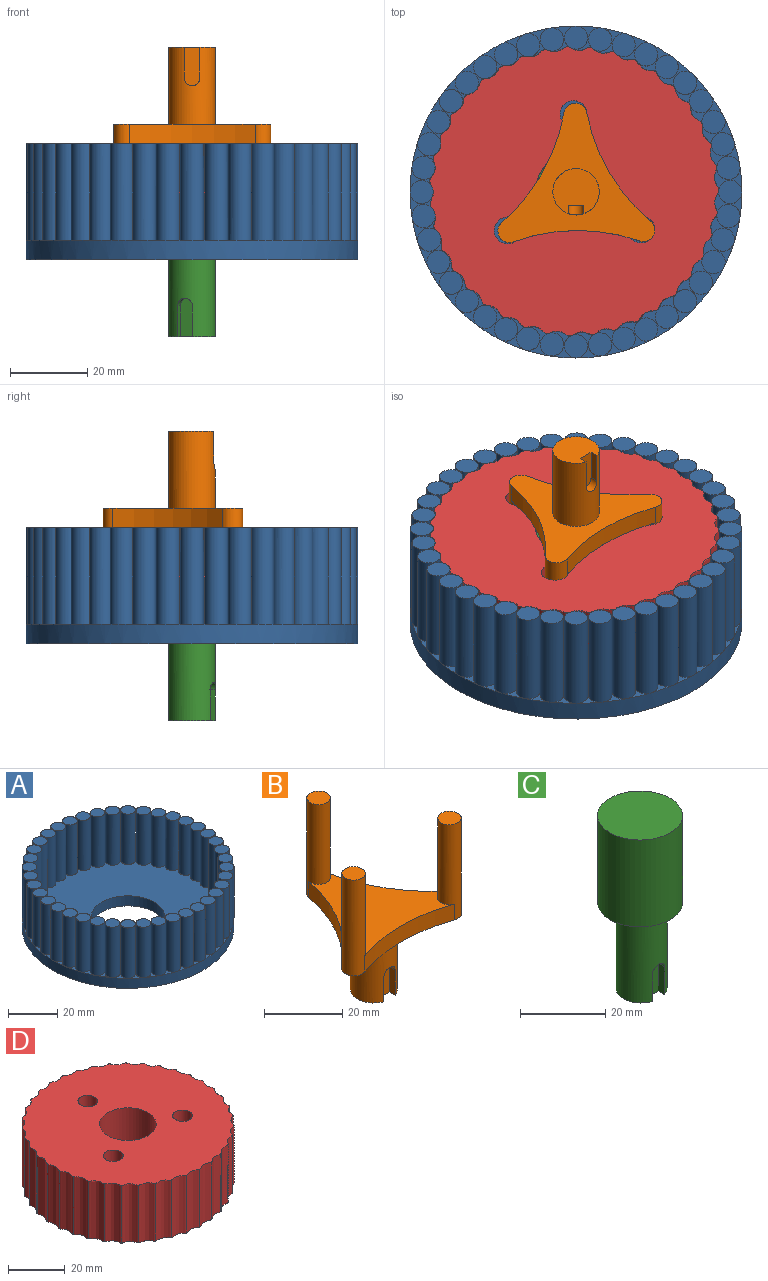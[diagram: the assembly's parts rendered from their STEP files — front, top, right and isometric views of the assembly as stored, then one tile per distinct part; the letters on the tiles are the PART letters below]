
ASSEMBLY  parts=4 mates=3
PART A: 84 faces, bbox 98x98x42 mm
  f0: cylinder r=15mm len=30mm, axis (0,0,1), area 471.2mm2, adj f2,f3
  f1: cylinder r=43mm len=86mm, axis (0,0,1), area 1350.9mm2, adj f2,f3
  f2: plane 86x86mm, normal (0,0,-1), area 5101.9mm2, adj f0,f1
  f3: plane 86x86mm, normal (0,0,1), area 3971mm2, adj f0,f1,f4,f6,f8,f10,f12,f14
  f4: cylinder r=3mm len=25mm, axis (0,0,-1), area 471.2mm2, adj f3,f5
  f5: plane 18x18mm, normal (0,0,1), area 56.5mm2, adj f4
  f6: cylinder r=3mm len=25mm, axis (0,0,-1), area 471.2mm2, adj f3,f7
  f7: plane 6x6mm, normal (0,0,1), area 28.3mm2, adj f6
  f8: cylinder r=3mm len=25mm, axis (0,0,-1), area 471.2mm2, adj f3,f9
  f9: plane 6x6mm, normal (0,0,1), area 28.3mm2, adj f8
  f10: cylinder r=3mm len=25mm, axis (0,0,-1), area 471.2mm2, adj f3,f11
  f11: plane 6x6mm, normal (0,0,1), area 28.3mm2, adj f10
  f12: cylinder r=3mm len=25mm, axis (0,0,-1), area 471.2mm2, adj f3,f13
  f13: plane 6x6mm, normal (0,0,1), area 28.3mm2, adj f12
  f14: cylinder r=3mm len=25mm, axis (0,0,-1), area 471.2mm2, adj f3,f15
  f15: plane 6x6mm, normal (0,0,1), area 28.3mm2, adj f14
  f16: cylinder r=3mm len=25mm, axis (0,0,-1), area 471.2mm2, adj f3,f17
  f17: plane 6x6mm, normal (0,0,1), area 28.3mm2, adj f16
  f18: cylinder r=3mm len=25mm, axis (0,0,-1), area 471.2mm2, adj f3,f19
  f19: plane 6x6mm, normal (0,0,1), area 28.3mm2, adj f18
  f20: cylinder r=3mm len=25mm, axis (0,0,-1), area 471.2mm2, adj f3,f21
  f21: plane 6x6mm, normal (0,0,1), area 28.3mm2, adj f20
  f22: cylinder r=3mm len=25mm, axis (0,0,-1), area 471.2mm2, adj f3,f23
  f23: plane 6x6mm, normal (0,0,1), area 28.3mm2, adj f22
  f24: cylinder r=3mm len=25mm, axis (0,0,-1), area 471.2mm2, adj f3,f25
  f25: plane 6x6mm, normal (0,0,1), area 28.3mm2, adj f24
  f26: cylinder r=3mm len=25mm, axis (0,0,-1), area 471.2mm2, adj f3,f27
  f27: plane 6x6mm, normal (0,0,1), area 28.3mm2, adj f26
  f28: cylinder r=3mm len=25mm, axis (0,0,-1), area 471.2mm2, adj f3,f29
  f29: plane 6x6mm, normal (0,0,1), area 28.3mm2, adj f28
  f30: cylinder r=3mm len=25mm, axis (0,0,-1), area 471.2mm2, adj f3,f31
  f31: plane 6x6mm, normal (0,0,1), area 28.3mm2, adj f30
  f32: cylinder r=3mm len=25mm, axis (0,0,-1), area 471.2mm2, adj f3,f33
  f33: plane 6x6mm, normal (0,0,1), area 28.3mm2, adj f32
  f34: cylinder r=3mm len=25mm, axis (0,0,-1), area 471.2mm2, adj f3,f35
  f35: plane 6x6mm, normal (0,0,1), area 28.3mm2, adj f34
  f36: cylinder r=3mm len=25mm, axis (0,0,-1), area 471.2mm2, adj f3,f37
  f37: plane 6x6mm, normal (0,0,1), area 28.3mm2, adj f36
  f38: cylinder r=3mm len=25mm, axis (0,0,-1), area 471.2mm2, adj f3,f39
  f39: plane 6x6mm, normal (0,0,1), area 28.3mm2, adj f38
  f40: cylinder r=3mm len=25mm, axis (0,0,-1), area 471.2mm2, adj f3,f41
  f41: plane 6x6mm, normal (0,0,1), area 28.3mm2, adj f40
  f42: cylinder r=3mm len=25mm, axis (0,0,-1), area 471.2mm2, adj f3,f43
  f43: plane 6x6mm, normal (0,0,1), area 28.3mm2, adj f42
  f44: cylinder r=3mm len=25mm, axis (0,0,-1), area 471.2mm2, adj f3,f45
  f45: plane 6x6mm, normal (0,0,1), area 28.3mm2, adj f44
  f46: cylinder r=3mm len=25mm, axis (0,0,-1), area 471.2mm2, adj f3,f47
  f47: plane 6x6mm, normal (0,0,1), area 28.3mm2, adj f46
  f48: cylinder r=3mm len=25mm, axis (0,0,-1), area 471.2mm2, adj f3,f49
  f49: plane 6x6mm, normal (0,0,1), area 28.3mm2, adj f48
  f50: cylinder r=3mm len=25mm, axis (0,0,-1), area 471.2mm2, adj f3,f51
  f51: plane 6x6mm, normal (0,0,1), area 28.3mm2, adj f50
  f52: cylinder r=3mm len=25mm, axis (0,0,-1), area 471.2mm2, adj f3,f53
  f53: plane 6x6mm, normal (0,0,1), area 28.3mm2, adj f52
  f54: cylinder r=3mm len=25mm, axis (0,0,-1), area 471.2mm2, adj f3,f55
  f55: plane 6x6mm, normal (0,0,1), area 28.3mm2, adj f54
  f56: cylinder r=3mm len=25mm, axis (0,0,-1), area 471.2mm2, adj f3,f57
  f57: plane 6x6mm, normal (0,0,1), area 28.3mm2, adj f56
  f58: cylinder r=3mm len=25mm, axis (0,0,-1), area 471.2mm2, adj f3,f59
  f59: plane 6x6mm, normal (0,0,1), area 28.3mm2, adj f58
  f60: cylinder r=3mm len=25mm, axis (0,0,-1), area 471.2mm2, adj f3,f61
  f61: plane 6x6mm, normal (0,0,1), area 28.3mm2, adj f60
  f62: cylinder r=3mm len=25mm, axis (0,0,-1), area 471.2mm2, adj f3,f63
  f63: plane 6x6mm, normal (0,0,1), area 28.3mm2, adj f62
  f64: cylinder r=3mm len=25mm, axis (0,0,-1), area 471.2mm2, adj f3,f65
  f65: plane 6x6mm, normal (0,0,1), area 28.3mm2, adj f64
  f66: cylinder r=3mm len=25mm, axis (0,0,-1), area 471.2mm2, adj f3,f67
  f67: plane 6x6mm, normal (0,0,1), area 28.3mm2, adj f66
  f68: cylinder r=3mm len=25mm, axis (0,0,-1), area 471.2mm2, adj f3,f69
  f69: plane 6x6mm, normal (0,0,1), area 28.3mm2, adj f68
  f70: cylinder r=3mm len=25mm, axis (0,0,-1), area 471.2mm2, adj f3,f71
  f71: plane 6x6mm, normal (0,0,1), area 28.3mm2, adj f70
  f72: cylinder r=3mm len=25mm, axis (0,0,-1), area 471.2mm2, adj f3,f73
  f73: plane 6x6mm, normal (0,0,1), area 28.3mm2, adj f72
  f74: cylinder r=3mm len=25mm, axis (0,0,-1), area 471.2mm2, adj f3,f75
  f75: plane 6x6mm, normal (0,0,1), area 28.3mm2, adj f74
  f76: cylinder r=3mm len=25mm, axis (0,0,-1), area 471.2mm2, adj f3,f77
  f77: plane 6x6mm, normal (0,0,1), area 28.3mm2, adj f76
  f78: cylinder r=3mm len=25mm, axis (0,0,-1), area 471.2mm2, adj f3,f79
  f79: plane 6x6mm, normal (0,0,1), area 28.3mm2, adj f78
  f80: cylinder r=3mm len=25mm, axis (0,0,-1), area 471.2mm2, adj f3,f81
  f81: plane 6x6mm, normal (0,0,1), area 28.3mm2, adj f80
  f82: cylinder r=3mm len=25mm, axis (0,0,-1), area 471.2mm2, adj f3,f83
  f83: plane 6x6mm, normal (0,0,1), area 28.3mm2, adj f82
PART B: 17 faces, bbox 40.6x36x50 mm
  f0: plane 12x11.66mm, normal (0,0,-1), area 103.5mm2, adj f12,f13,f14,f15
  f1: cylinder r=48.5mm len=28.25mm, axis (0,0,1), area 166.4mm2, adj f2,f6,f7,f8
  f2: cylinder r=3mm len=30mm, axis (0,0,1), area 512.9mm2, adj f1,f3,f7,f8,f9
  f3: cylinder r=48.5mm len=28.25mm, axis (0,0,1), area 166.4mm2, adj f2,f4,f7,f8
  f4: cylinder r=3mm len=30mm, axis (0,0,1), area 512.9mm2, adj f3,f5,f7,f8,f10
  f5: cylinder r=48.5mm len=32.62mm, axis (0,0,1), area 166.4mm2, adj f4,f6,f7,f8
  f6: cylinder r=3mm len=30mm, axis (0,0,1), area 512.9mm2, adj f1,f5,f7,f8,f11
  f7: plane 40.64x36mm, normal (0,0,-1), area 543.7mm2, adj f1,f2,f3,f4,f5,f6,f12
  f8: plane 38.53x33.36mm, normal (0,0,1), area 571.9mm2, adj f1,f2,f3,f4,f5,f6
  f9: plane 6x6mm, normal (0,0,1), area 28.3mm2, adj f2
  f10: plane 6x6mm, normal (0,0,1), area 28.3mm2, adj f4
  f11: plane 6x6mm, normal (0,0,1), area 28.3mm2, adj f6
  f12: cylinder r=6mm len=20mm, axis (0,0,1), area 715mm2, adj f0,f7,f13,f15,f16
  f13: plane 8x2.16mm, normal (1,0,0), area 17.3mm2, adj f0,f12,f14,f16
  f14: plane 10x4mm, normal (0,-1,0), area 38.3mm2, adj f0,f13,f15,f16
  f15: plane 8x2.16mm, normal (-1,0,0), area 17.3mm2, adj f0,f12,f14,f16
  f16: cylinder r=2mm len=4mm, axis (0,1,0), area 14.6mm2, adj f12,f13,f14,f15
PART C: 9 faces, bbox 20x20x50 mm
  f0: plane 12x11.66mm, normal (0,0,-1), area 103.5mm2, adj f4,f5,f6,f7
  f1: cylinder r=10mm len=25mm, axis (0,0,-1), area 1570.8mm2, adj f2,f3
  f2: plane 20x20mm, normal (0,0,1), area 314.2mm2, adj f1
  f3: plane 20x20mm, normal (0,0,-1), area 201.1mm2, adj f1,f4
  f4: cylinder r=6mm len=25mm, axis (0,0,1), area 903.5mm2, adj f0,f3,f5,f7,f8
  f5: plane 8x2.16mm, normal (1,0,0), area 17.3mm2, adj f0,f4,f6,f8
  f6: plane 10x4mm, normal (0,-1,0), area 38.3mm2, adj f0,f5,f7,f8
  f7: plane 8x2.16mm, normal (-1,0,0), area 17.3mm2, adj f0,f4,f6,f8
  f8: cylinder r=2mm len=4mm, axis (0,1,0), area 14.6mm2, adj f4,f5,f6,f7
PART D: 45 faces, bbox 74.9x74.9x25 mm
  f0: extruded ~25x4.52mm, area 164mm2, adj f1,f38,f39,f40
  f1: extruded ~25x4.67mm, area 164mm2, adj f0,f2,f39,f40
  f2: extruded ~25x5.23mm, area 164mm2, adj f1,f3,f39,f40
  f3: extruded ~25x5.64mm, area 164mm2, adj f2,f4,f39,f40
  f4: extruded ~25x5.91mm, area 164mm2, adj f3,f5,f39,f40
  f5: extruded ~25x6.03mm, area 164mm2, adj f4,f6,f39,f40
  f6: extruded ~25x5.99mm, area 164mm2, adj f5,f7,f39,f40
  f7: extruded ~25x5.8mm, area 164mm2, adj f6,f8,f39,f40
  f8: extruded ~25x5.45mm, area 164mm2, adj f7,f9,f39,f40
  f9: extruded ~25x4.97mm, area 164mm2, adj f8,f10,f39,f40
  f10: extruded ~25x4.35mm, area 164mm2, adj f9,f11,f39,f40
  f11: extruded ~25x4.82mm, area 164mm2, adj f10,f12,f39,f40
  f12: extruded ~25x5.34mm, area 164mm2, adj f11,f13,f39,f40
  f13: extruded ~25x5.72mm, area 164mm2, adj f12,f14,f39,f40
  f14: extruded ~25x5.96mm, area 164mm2, adj f13,f15,f39,f40
  f15: extruded ~25x6.04mm, area 164mm2, adj f14,f16,f39,f40
  f16: extruded ~25x5.96mm, area 164mm2, adj f15,f17,f39,f40
  f17: extruded ~25x5.72mm, area 164mm2, adj f16,f18,f39,f40
  f18: extruded ~25x5.34mm, area 164mm2, adj f17,f19,f39,f40
  f19: extruded ~25x4.82mm, area 164mm2, adj f18,f20,f39,f40
  f20: extruded ~25x4.35mm, area 164mm2, adj f19,f21,f39,f40
  f21: extruded ~25x4.97mm, area 164mm2, adj f20,f22,f39,f40
  f22: extruded ~25x5.45mm, area 164mm2, adj f21,f23,f39,f40
  f23: extruded ~25x5.8mm, area 164mm2, adj f22,f24,f39,f40
  f24: extruded ~25x5.99mm, area 164mm2, adj f23,f25,f39,f40
  f25: extruded ~25x6.03mm, area 164mm2, adj f24,f26,f39,f40
  f26: extruded ~25x5.91mm, area 164mm2, adj f25,f27,f39,f40
  f27: extruded ~25x5.64mm, area 164mm2, adj f26,f28,f39,f40
  f28: extruded ~25x5.23mm, area 164mm2, adj f27,f29,f39,f40
  f29: extruded ~25x4.67mm, area 164mm2, adj f28,f30,f39,f40
  f30: extruded ~25x4.52mm, area 164mm2, adj f29,f31,f39,f40
  f31: extruded ~25x5.1mm, area 164mm2, adj f30,f32,f39,f40
  f32: extruded ~25x5.55mm, area 164mm2, adj f31,f33,f39,f40
  f33: extruded ~25x5.86mm, area 164mm2, adj f32,f34,f39,f40
  f34: extruded ~25x6.02mm, area 164mm2, adj f33,f35,f39,f40
  f35: extruded ~25x6.02mm, area 164mm2, adj f34,f36,f39,f40
  f36: extruded ~25x5.86mm, area 164mm2, adj f35,f37,f39,f40
  f37: extruded ~25x5.55mm, area 164mm2, adj f36,f38,f39,f40
  f38: extruded ~25x5.1mm, area 164mm2, adj f0,f37,f39,f40
  f39: plane 74.94x74.88mm, normal (0,0,1), area 3851.7mm2, adj f0,f1,f2,f3,f4,f5,f6,f7
  f40: plane 74.94x74.88mm, normal (0,0,-1), area 3851.7mm2, adj f0,f1,f2,f3,f4,f5,f6,f7
  f41: cylinder r=10mm len=25mm, axis (0,0,-1), area 1570.8mm2, adj f39,f40
  f42: cylinder r=3.5mm len=25mm, axis (0,0,-1), area 549.8mm2, adj f39,f40
  f43: cylinder r=3.5mm len=25mm, axis (0,0,-1), area 549.8mm2, adj f39,f40
  f44: cylinder r=3.5mm len=25mm, axis (0,0,-1), area 549.8mm2, adj f39,f40
PLACE A at identity fixed
PLACE B rot(axis=(0,-1,0),180deg) t=(0,0,25)mm
PLACE C rot(axis=(0,0,-1),18.4deg) t=(-0.47,0.16,0)mm
PLACE D rot(axis=(0,0,1),0.5deg) t=(-0.47,0.16,0)mm
MATE revolute D.f41 <-> C.f1  axis (0,0,1) through (-0.47,0.16,25)mm
MATE revolute C.f4 <-> A.f0  axis (0,0,-1) through (0,0,0)mm
MATE revolute C.f4 <-> B.f12  axis (0,0,-1) through (0,0,0)mm
